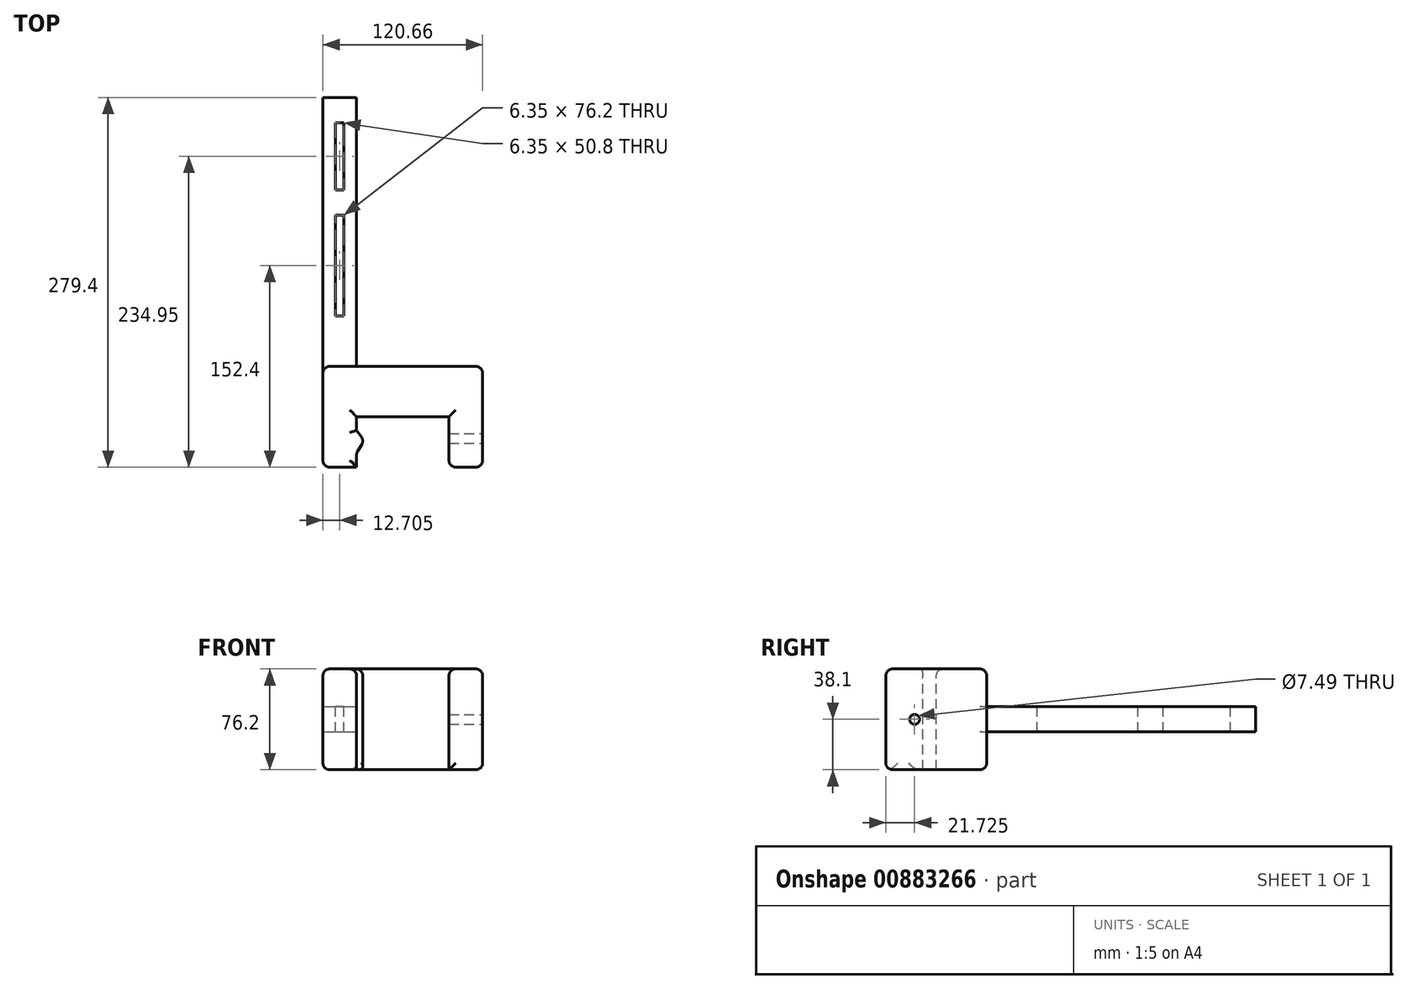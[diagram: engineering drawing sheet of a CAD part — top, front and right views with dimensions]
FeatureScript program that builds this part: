
annotation { "Feature Type Name" : "Feature", "Feature Type Description" : "" }
export const myFeature = defineFeature(function(context is Context, id is Id, definition is map)
    precondition{}
    {
        {
            var Q0;
            Q0=qCreatedBy(makeId("Top.planeOp"),FACE);
            var sketch = newSketch(context, id + "F0", { "sketchPlane" : qUnion([Q0])});
            skLineSegment(sketch, "E0.bottom", {"start": v(60.33, -38.1) * mm, "end": v(-60.32, -38.1) * mm});
            skLineSegment(sketch, "E0.top", {"start": v(60.33, 38.1) * mm, "end": v(-60.33, 38.1) * mm});
            skLineSegment(sketch, "E0.left", {"start": v(60.33, -38.1) * mm, "end": v(60.33, 38.1) * mm});
            skLineSegment(sketch, "E0.right", {"start": v(-60.32, -38.1) * mm, "end": v(-60.33, 38.1) * mm});
            skPoint(sketch, "E0.middle", {"position": v(0, 0) * mm});
            skSolve(sketch);
        }
        {
            var Q0;
            Q0=makeQuery(id+"F0.imprint","IMPRINT",FACE,{"disambiguationData":[TD([[makeQuery(id+"F0.imprint","IMPRINT",EDGE,{"derivedFrom":sQuery(id+"F0.wireOp",EDGE,"E0.bottom")}),-1.0]])]});
            var sketch = newSketch(context, id + "F1", { "sketchPlane" : qUnion([Q0])});
            skLineSegment(sketch, "E1.bottom", {"start": v(34.92, -101.6) * mm, "end": v(-34.93, -101.6) * mm});
            skLineSegment(sketch, "E1.top", {"start": v(34.93, 0) * mm, "end": v(-34.92, 0) * mm});
            skLineSegment(sketch, "E1.left", {"start": v(34.92, -101.6) * mm, "end": v(34.93, 0) * mm});
            skLineSegment(sketch, "E1.right", {"start": v(-34.93, -101.6) * mm, "end": v(-34.92, 0) * mm});
            skPoint(sketch, "E1.middle", {"position": v(0, -50.8) * mm});
            skSolve(sketch);
        }
        {
            var Q0;
            Q0 = qSketchRegion(id + "F0", true);
            extrude(context, id + "F2", {"entities" : qUnion([Q0]), "depth" : 76.2 * mm, "offsetDistance" : 25.4 * mm, "symmetric" : true});
        }
        {
            var Q0;
            Q0 = qSketchRegion(id + "F1", true);
            extrude(context, id + "F3", {"entities" : qUnion([Q0]), "operationType" : NewBodyOperationType.REMOVE, "oppositeDirection" : true, "depth" : 76.2 * mm, "offsetDistance" : 25.4 * mm, "symmetric" : true});
        }
        {
            var Q0;
            Q0=makeQuery(id+"F2.opExtrude","SWEPT_FACE",FACE,{"disambiguationData":[OSD([sQuery(id+"F0.wireOp",EDGE,"E0.left")])]});
            var sketch = newSketch(context, id + "F4", { "sketchPlane" : qUnion([Q0])});
            skCircle(sketch, "E2", {"center": v(-16.38, 0) * mm, "radius": 3.75 * mm});
            skSolve(sketch);
        }
        {
            var Q0;
            Q0 = qSketchRegion(id + "F4", true);
            extrude(context, id + "F5", {"entities" : qUnion([Q0]), "operationType" : NewBodyOperationType.REMOVE, "oppositeDirection" : true, "depth" : 76.2 * mm, "offsetDistance" : 25.4 * mm, "symmetric" : true});
        }
        {
            var Q0;
            Q0=makeQuery(id+"F2.opExtrude","SWEPT_FACE",FACE,{"disambiguationData":[OSD([sQuery(id+"F0.wireOp",EDGE,"E0.top")])]});
            var sketch = newSketch(context, id + "F6", { "sketchPlane" : qUnion([Q0])});
            skLineSegment(sketch, "E3.bottom", {"start": v(60.32, -9.53) * mm, "end": v(34.92, -9.53) * mm});
            skLineSegment(sketch, "E3.top", {"start": v(60.32, 9.52) * mm, "end": v(34.92, 9.52) * mm});
            skLineSegment(sketch, "E3.left", {"start": v(60.33, -9.53) * mm, "end": v(60.33, 9.52) * mm});
            skLineSegment(sketch, "E3.right", {"start": v(34.92, -9.53) * mm, "end": v(34.92, 9.52) * mm});
            skPoint(sketch, "E3.middle", {"position": v(47.62, 0) * mm});
            skPoint(sketch, "E3.middle.positionSnap0", {"position": v(60.33, 0) * mm});
            skPoint(sketch, "E3.centerSnap0", {"position": v(60.33, 0) * mm});
            skSolve(sketch);
        }
        {
            var Q0;
            Q0=makeQuery(id+"F6.imprint","IMPRINT",FACE,{"disambiguationData":[TD([[makeQuery(id+"F6.imprint","IMPRINT",EDGE,{"derivedFrom":sQuery(id+"F6.wireOp",EDGE,"E3.bottom")}),-1.0]])]});
            extrude(context, id + "F7", {"entities" : qUnion([Q0]), "operationType" : NewBodyOperationType.ADD, "depth" : 203.2 * mm, "offsetDistance" : 25.4 * mm});
        }
        {
            var Q0;
            Q0=makeQuery(id+"F7.opExtrude","SWEPT_FACE",FACE,{"disambiguationData":[OSD([sQuery(id+"F6.wireOp",EDGE,"E3.top")])]});
            var sketch = newSketch(context, id + "F8", { "sketchPlane" : qUnion([Q0])});
            skLineSegment(sketch, "E4.bottom", {"start": v(-44.45, 152.4) * mm, "end": v(-50.8, 152.4) * mm});
            skLineSegment(sketch, "E4.top", {"start": v(-44.45, 76.2) * mm, "end": v(-50.8, 76.2) * mm});
            skLineSegment(sketch, "E4.left", {"start": v(-44.45, 152.4) * mm, "end": v(-44.45, 76.2) * mm});
            skLineSegment(sketch, "E4.right", {"start": v(-50.8, 152.4) * mm, "end": v(-50.8, 76.2) * mm});
            skPoint(sketch, "E4.middle", {"position": v(-47.62, 114.3) * mm});
            skLineSegment(sketch, "E5.bottom", {"start": v(-44.45, 171.45) * mm, "end": v(-50.8, 171.45) * mm});
            skLineSegment(sketch, "E5.top", {"start": v(-44.45, 222.25) * mm, "end": v(-50.8, 222.25) * mm});
            skLineSegment(sketch, "E5.left", {"start": v(-44.45, 171.45) * mm, "end": v(-44.45, 222.25) * mm});
            skLineSegment(sketch, "E5.right", {"start": v(-50.8, 171.45) * mm, "end": v(-50.8, 222.25) * mm});
            skPoint(sketch, "E5.middle", {"position": v(-47.63, 196.85) * mm});
            skPoint(sketch, "E6.orphan", {"position": v(-47.63, 241.3) * mm});
            skPoint(sketch, "E7.end.orphan", {"position": v(-47.62, 38.1) * mm});
            skSolve(sketch);
        }
        {
            var Q0;
            Q0=makeQuery(id+"F8.imprint","IMPRINT",FACE,{"disambiguationData":[TD([[makeQuery(id+"F8.imprint","IMPRINT",EDGE,{"derivedFrom":sQuery(id+"F8.wireOp",EDGE,"E5.bottom")}),-1.0]])]});
            var Q1;
            Q1=makeQuery(id+"F8.imprint","IMPRINT",FACE,{"disambiguationData":[TD([[makeQuery(id+"F8.imprint","IMPRINT",EDGE,{"derivedFrom":sQuery(id+"F8.wireOp",EDGE,"E4.bottom")}),1.0]])]});
            extrude(context, id + "F9", {"entities" : qUnion([Q0, Q1]), "operationType" : NewBodyOperationType.REMOVE, "endBound" : BoundingType.THROUGH_ALL, "oppositeDirection" : true, "depth" : 25.4 * mm, "offsetDistance" : 25.4 * mm});
        }
        {
            var Q0;
            Q0=qCreatedBy(makeId("Top.planeOp"),FACE);
            var sketch = newSketch(context, id + "F10", { "sketchPlane" : qUnion([Q0])});
            skLineSegment(sketch, "E8", {"start": v(-34.99, -10.16) * mm, "end": v(-29.3, -18.02) * mm});
            skLineSegment(sketch, "E9", {"start": v(-29.3, -18.02) * mm, "end": v(-35.06, -27.81) * mm});
            skLineSegment(sketch, "E10", {"start": v(-35.06, -27.81) * mm, "end": v(-34.99, -10.16) * mm});
            skSolve(sketch);
        }
        {
            var Q0;
            Q0=makeQuery(id+"F10.imprint","IMPRINT",FACE,{"disambiguationData":[TD([[makeQuery(id+"F10.imprint","IMPRINT",EDGE,{"derivedFrom":sQuery(id+"F10.wireOp",EDGE,"E8")}),-1.0]])]});
            extrude(context, id + "F11", {"entities" : qUnion([Q0]), "operationType" : NewBodyOperationType.ADD, "depth" : 76.2 * mm, "offsetDistance" : 25.4 * mm, "symmetric" : true});
        }
        {
            var Q0;
            Q0=makeQuery(id+"F2.opExtrude","SWEPT_EDGE",EDGE,{"disambiguationData":[OSD([sQuery(id+"F0.wireOp",EDGE,"E0.bottom"),sQuery(id+"F0.wireOp",EDGE,"E0.left")])]});
            var Q1;
            Q1=makeQuery(id+"F2.opExtrude","CAP_EDGE",EDGE,{"disambiguationData":[OSD([sQuery(id+"F0.wireOp",EDGE,"E0.left")])],"isStart":false});
            var Q2;
            Q2=makeQuery(id+"F2.opExtrude","SWEPT_EDGE",EDGE,{"disambiguationData":[OSD([sQuery(id+"F0.wireOp",EDGE,"E0.top"),sQuery(id+"F0.wireOp",EDGE,"E0.left")])]});
            var Q3;
            Q3=makeQuery(id+"F2.opExtrude","CAP_EDGE",EDGE,{"disambiguationData":[OSD([sQuery(id+"F0.wireOp",EDGE,"E0.left")])],"isStart":true});
            var Q4;
            Q4=makeQuery(id+"F2.opExtrude","CAP_EDGE",EDGE,{"disambiguationData":[OSD([sQuery(id+"F0.wireOp",EDGE,"E0.top")])],"isStart":false});
            var Q5;
            {var subQ0=sQuery(id+"F0.wireOp",EDGE,"E0.right");var subQ1=sQuery(id+"F0.wireOp",EDGE,"E0.top");Q5=makeQuery(id+"F7.boolean.opBoolean","SPLIT",EDGE,{"disambiguationData":[TD([makeQuery(id+"F7.opExtrude","SWEPT_FACE",FACE,{"disambiguationData":[OSD([sQuery(id+"F6.wireOp",EDGE,"E3.top")])]})])],"derivedFrom":makeQuery(id+"F2.opExtrude","SWEPT_EDGE",EDGE,{"disambiguationData":[OSD([subQ1,subQ0])]})});}
            var Q6;
            {var subQ0=sQuery(id+"F0.wireOp",EDGE,"E0.top");var subQ1=sQuery(id+"F0.wireOp",EDGE,"E0.right");Q6=makeQuery(id+"F7.boolean.opBoolean","SPLIT",EDGE,{"disambiguationData":[TD([makeQuery(id+"F7.opExtrude","SWEPT_FACE",FACE,{"disambiguationData":[OSD([sQuery(id+"F6.wireOp",EDGE,"E3.bottom")])]})])],"derivedFrom":makeQuery(id+"F2.opExtrude","SWEPT_EDGE",EDGE,{"disambiguationData":[OSD([subQ0,subQ1])]})});}
            var Q7;
            Q7=makeQuery(id+"F2.opExtrude","CAP_EDGE",EDGE,{"disambiguationData":[OSD([sQuery(id+"F0.wireOp",EDGE,"E0.top")])],"isStart":true});
            var Q8;
            Q8=makeQuery(id+"F2.opExtrude","CAP_EDGE",EDGE,{"disambiguationData":[OSD([sQuery(id+"F0.wireOp",EDGE,"E0.right")])],"isStart":false});
            var Q9;
            Q9=makeQuery(id+"F2.opExtrude","SWEPT_EDGE",EDGE,{"disambiguationData":[OSD([sQuery(id+"F0.wireOp",EDGE,"E0.bottom"),sQuery(id+"F0.wireOp",EDGE,"E0.right")])]});
            var Q10;
            Q10=makeQuery(id+"F2.opExtrude","CAP_EDGE",EDGE,{"disambiguationData":[OSD([sQuery(id+"F0.wireOp",EDGE,"E0.right")])],"isStart":true});
            var Q11;
            Q11=makeQuery(id+"F3.boolean.opBoolean","INTERSECT",EDGE,{"derivedFrom":[makeQuery(id+"F2.opExtrude","SWEPT_FACE",FACE,{"disambiguationData":[OSD([sQuery(id+"F0.wireOp",EDGE,"E0.bottom")])]}),makeQuery(id+"F3.opExtrude","SWEPT_FACE",FACE,{"disambiguationData":[OSD([sQuery(id+"F1.wireOp",EDGE,"E1.left")])]})]});
            var Q12;
            Q12=makeQuery(id+"F11.opExtrude","SWEPT_FACE",FACE,{"disambiguationData":[OSD([sQuery(id+"F10.wireOp",EDGE,"E9")])]});
            var Q13;
            Q13=makeQuery(id+"F3.boolean.opBoolean","COPY",EDGE,{"derivedFrom":makeQuery(id+"F3.opExtrude","CAP_EDGE",EDGE,{"disambiguationData":[OSD([sQuery(id+"F1.wireOp",EDGE,"E1.top")])],"isStart":true})});
            var Q14;
            Q14=makeQuery(id+"F3.boolean.opBoolean","COPY",EDGE,{"derivedFrom":makeQuery(id+"F3.opExtrude","CAP_EDGE",EDGE,{"disambiguationData":[OSD([sQuery(id+"F1.wireOp",EDGE,"E1.top")])],"isStart":false})});
            var Q15;
            {var subQ1=sQuery(id+"F0.wireOp",EDGE,"E0.left");var subQ3=sQuery(id+"F0.wireOp",EDGE,"E0.bottom");Q15=makeQuery(id+"F3.boolean.opBoolean","SPLIT",FACE,{"disambiguationData":[TD([makeQuery(id+"F2.opExtrude","SWEPT_FACE",FACE,{"disambiguationData":[OSD([subQ1])]})])],"derivedFrom":makeQuery(id+"F2.opExtrude","SWEPT_FACE",FACE,{"disambiguationData":[OSD([subQ3])]})});}
            var Q16;
            {var subQ0=sQuery(id+"F0.wireOp",EDGE,"E0.bottom");var subQ1=sQuery(id+"F0.wireOp",EDGE,"E0.right");Q16=makeQuery(id+"F3.boolean.opBoolean","SPLIT",EDGE,{"disambiguationData":[TD([makeQuery(id+"F2.opExtrude","SWEPT_FACE",FACE,{"disambiguationData":[OSD([subQ1])]})])],"derivedFrom":makeQuery(id+"F2.opExtrude","CAP_EDGE",EDGE,{"disambiguationData":[OSD([subQ0])],"isStart":false})});}
            var Q17;
            {var subQ0=sQuery(id+"F0.wireOp",EDGE,"E0.bottom");var subQ1=sQuery(id+"F0.wireOp",EDGE,"E0.right");Q17=makeQuery(id+"F3.boolean.opBoolean","SPLIT",EDGE,{"disambiguationData":[TD([makeQuery(id+"F2.opExtrude","SWEPT_FACE",FACE,{"disambiguationData":[OSD([subQ1])]})])],"derivedFrom":makeQuery(id+"F2.opExtrude","CAP_EDGE",EDGE,{"disambiguationData":[OSD([subQ0])],"isStart":true})});}
            var Q18;
            {var subQ0=sQuery(id+"F1.wireOp",EDGE,"E1.right");Q18=makeQuery(id+"F11.boolean.opBoolean","SPLIT",EDGE,{"disambiguationData":[TD([makeQuery(id+"F3.boolean.opBoolean","COPY",FACE,{"derivedFrom":makeQuery(id+"F3.opExtrude","SWEPT_FACE",FACE,{"disambiguationData":[OSD([sQuery(id+"F1.wireOp",EDGE,"E1.top")])]})})])],"derivedFrom":makeQuery(id+"F3.boolean.opBoolean","COPY",EDGE,{"derivedFrom":makeQuery(id+"F3.opExtrude","CAP_EDGE",EDGE,{"disambiguationData":[OSD([subQ0])],"isStart":true})})});}
            var Q19;
            Q19=makeQuery(id+"F11.opExtrude","CAP_EDGE",EDGE,{"disambiguationData":[OSD([sQuery(id+"F10.wireOp",EDGE,"E8")])],"isStart":false});
            var Q20;
            Q20=makeQuery(id+"F11.boolean.opBoolean","MERGE",FACE,{"derivedFrom":[makeQuery(id+"F2.opExtrude","CAP_FACE",FACE,{"disambiguationData":[OSD([sQuery(id+"F0.wireOp",EDGE,"E0.bottom"),sQuery(id+"F0.wireOp",EDGE,"E0.top"),sQuery(id+"F0.wireOp",EDGE,"E0.left"),sQuery(id+"F0.wireOp",EDGE,"E0.right")])],"isStart":false}),makeQuery(id+"F11.opExtrude","CAP_FACE",FACE,{"disambiguationData":[OSD([sQuery(id+"F10.wireOp",EDGE,"E8"),sQuery(id+"F10.wireOp",EDGE,"E9"),sQuery(id+"F10.wireOp",EDGE,"E10")])],"isStart":false})]});
            fillet(context, id + "F12", {"entities" : qUnion([Q0, Q1, Q2, Q3, Q4, Q5, Q6, Q7, Q8, Q9, Q10, Q11, Q12, Q13, Q14, Q15, Q16, Q17, Q18, Q19, Q20]), "radius" : 5.08 * mm, "tangentPropagation" : true, "allowEdgeOverflow" : false});
        }
    });
